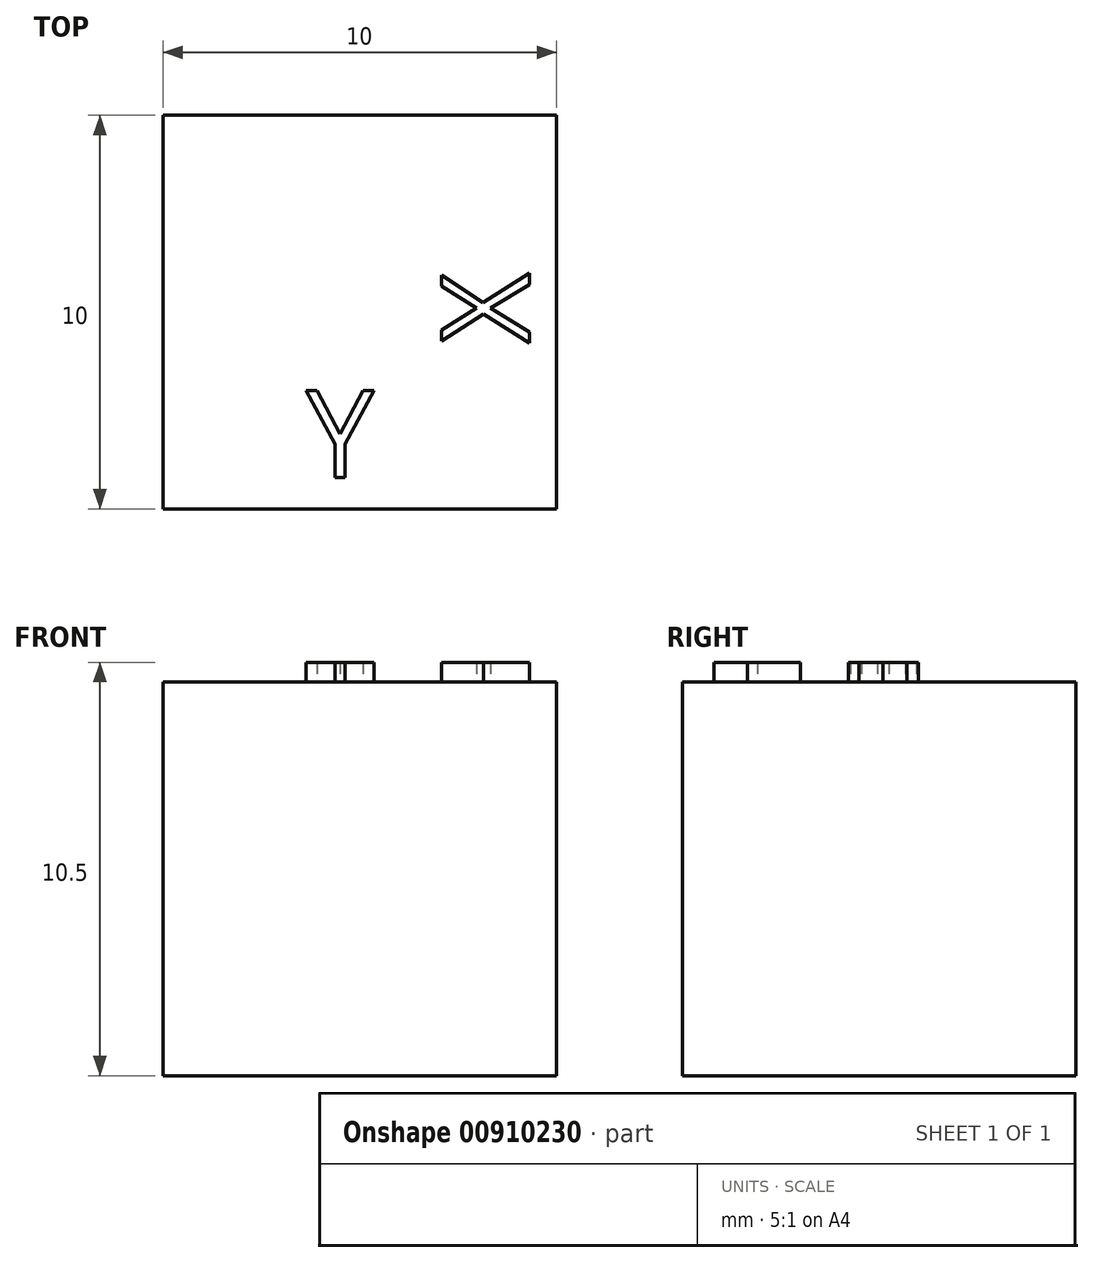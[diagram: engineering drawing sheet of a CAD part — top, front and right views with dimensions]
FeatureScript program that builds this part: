
annotation { "Feature Type Name" : "Feature", "Feature Type Description" : "" }
export const myFeature = defineFeature(function(context is Context, id is Id, definition is map)
    precondition{}
    {
        {
            var Q0;
            Q0=qCreatedBy(makeId("Top.planeOp"),FACE);
            var sketch = newSketch(context, id + "F0", { "sketchPlane" : qUnion([Q0])});
            skLineSegment(sketch, "E0.bottom", {"start": v(-1.1, -6.28) * mm, "end": v(8.9, -6.28) * mm});
            skLineSegment(sketch, "E0.top", {"start": v(-1.1, 3.72) * mm, "end": v(8.9, 3.72) * mm});
            skLineSegment(sketch, "E0.left", {"start": v(-1.1, -6.28) * mm, "end": v(-1.1, 3.72) * mm});
            skLineSegment(sketch, "E0.right", {"start": v(8.9, -6.28) * mm, "end": v(8.9, 3.72) * mm});
            skSolve(sketch);
        }
        {
            var Q0;
            Q0=makeQuery(id+"F0.imprint","IMPRINT",FACE,{"disambiguationData":[TD([[makeQuery(id+"F0.imprint","IMPRINT",EDGE,{"derivedFrom":sQuery(id+"F0.wireOp",EDGE,"E0.bottom")}),1.0]])]});
            extrude(context, id + "F1", {"entities" : qUnion([Q0]), "depth" : 10 * mm, "offsetDistance" : 25 * mm});
        }
        {
            var Q0;
            Q0=makeQuery(id+"F1.opExtrude","CAP_FACE",FACE,{"disambiguationData":[OSD([sQuery(id+"F0.wireOp",EDGE,"E0.bottom"),sQuery(id+"F0.wireOp",EDGE,"E0.top"),sQuery(id+"F0.wireOp",EDGE,"E0.left"),sQuery(id+"F0.wireOp",EDGE,"E0.right")])],"isStart":false});
            var sketch = newSketch(context, id + "F2", { "sketchPlane" : qUnion([Q0])});
            skText(sketch, "E1", { "text": "Y", "fontName": "OpenSans-Regular.ttf"});
            skText(sketch, "E2", { "text": "X", "fontName": "OpenSans-Regular.ttf"});
            const initialGuessF2  = {"E1": [0.00254, -0.00548, 1, 0, 0.00222], "E2": [0.00821, -0.00208, 0, 1, 0.00225]};
            skSetInitialGuess(sketch, initialGuessF2);
            skSolve(sketch);
        }
        {
            var Q0;
            Q0 = qSketchRegion(id + "F2", true);
            extrude(context, id + "F3", {"entities" : qUnion([Q0]), "operationType" : NewBodyOperationType.ADD, "depth" : 0.5 * mm, "offsetDistance" : 25 * mm});
        }
    });
